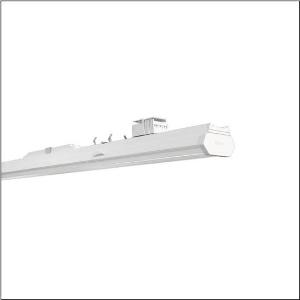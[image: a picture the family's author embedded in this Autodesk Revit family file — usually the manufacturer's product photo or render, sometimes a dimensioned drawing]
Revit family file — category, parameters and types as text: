
# Revit family: licross_r__11_protected_mo_51td12dn495g3s_4e23
name_source: partatom
category: Lighting Fixtures
units: mm (PartAtom-declared; Revit-internal decimal feet)

## family parameters
Cut with Voids When Loaded = No
Host = Face
Light Source = No
Part Type = Normal
Room Calculation Point = No
Round Connector Dimension = Use Diameter
Shared = No

## types (1)
- --- (1 x LED, 980 lm, 6.8 W, 4000K)
    Apparent Load = 7 VA
    CIE Flux Codes = 73 92 98 99 100
    Color Rendering = 80
    Color Temperature = 4000K
    Default Elevation = 1800 mm
    Description = Licross® 11 Protected MO, luminaire insert, of sheet steel, galvanised, coil coated, white, length: 1.500mm, width: 90mm, height: 101mm, LED rated luminous flux: 9.980lm, light colour: 840, SDCM (Standard Deviation of Colour Matching)MacAdam ≤ 2 SDCM (initial), control gear: DALI 2 (for two DALI lines), with plug, 6-pole, with phase selection, for trunking rail, 14-core, mains connection: 220..240V, AC, 50/60Hz, rated input power: 61W, for trunking rail, 14-core, internal wiring halogen-free, for emergency light function, converter,control gear: single battery element, battery: LiFePO4, 9Ah, primary light control with lens, of plastic, primary optical cover: cover, of PMMA, light emission: direct distribution, primary light characteristic: symmetric, protection rating (complete): IP54, insulation class (complete): insulation class I (protective earthing), certification: CE, UKCA, protection symbol: D if used in an environment with non-conductive dust loads with corresponding accessories, impact resistance: IK06, permissible ambient temperature for indoor applications: +5..+35°C, standard: EN 60598-2-22, LABS conformity tested according to VDMA 24364:2018-05, reducing of maximum allowable ambient temperature of 5°C with ceiling mounting, corresponds to IFS (International Featured Standards) requirements for safety and quality in the food industry, packaging unit: 1 piece
    Height = 92 mm
    Lamp = 1 x LED
    Lamp Light Flux = 980 lm
    Lamp Power = 6.8 W
    Lamp count = 1
    Length = 1500 mm
    Luminous efficacy = 144 lm/W
    Manufacturer = Siteco
    ModVariant = No
    Model = 51TD12DN495G3S
    Mounting Place = Ceiling
    Mounting Type = Pendant
    Number of Poles = 1
    OnlyDefault = Yes
    Power Factor = 1
    Product Name = Licross® 11 Protected MO
    Product group = luminaire insert | ceiling pendant
    ProductGroupID = 901
    Protection Class = Protection class I
    Protection Degree = IP 54
    RLX_Detail_Level = 1
    RLX_Emergency_Light_Flux = 0 lm
    RLX_Emergency_Type = 0
    RLX_Emergency_Type_DB = No
    RlxData = <blob elided: 25005 chars, md5=5aaf4667>
    Socket = socket
    Standby Power = 0 W
    System Light Flux = 980 lm
    System Power = 7 W
    Type Comments = : emergency light operation: 3 h
    Type Image = l_1256145.jpg
    URL = http://relux.com
    VarID = @adj_098529
    Voltage = 0 V
    Weight = 0.00 kg
    Width = 88 mm

## geometry (parser evidence)
native form markers: Blend x4, Sweep x12
no freeform markers — native parametric forms only
